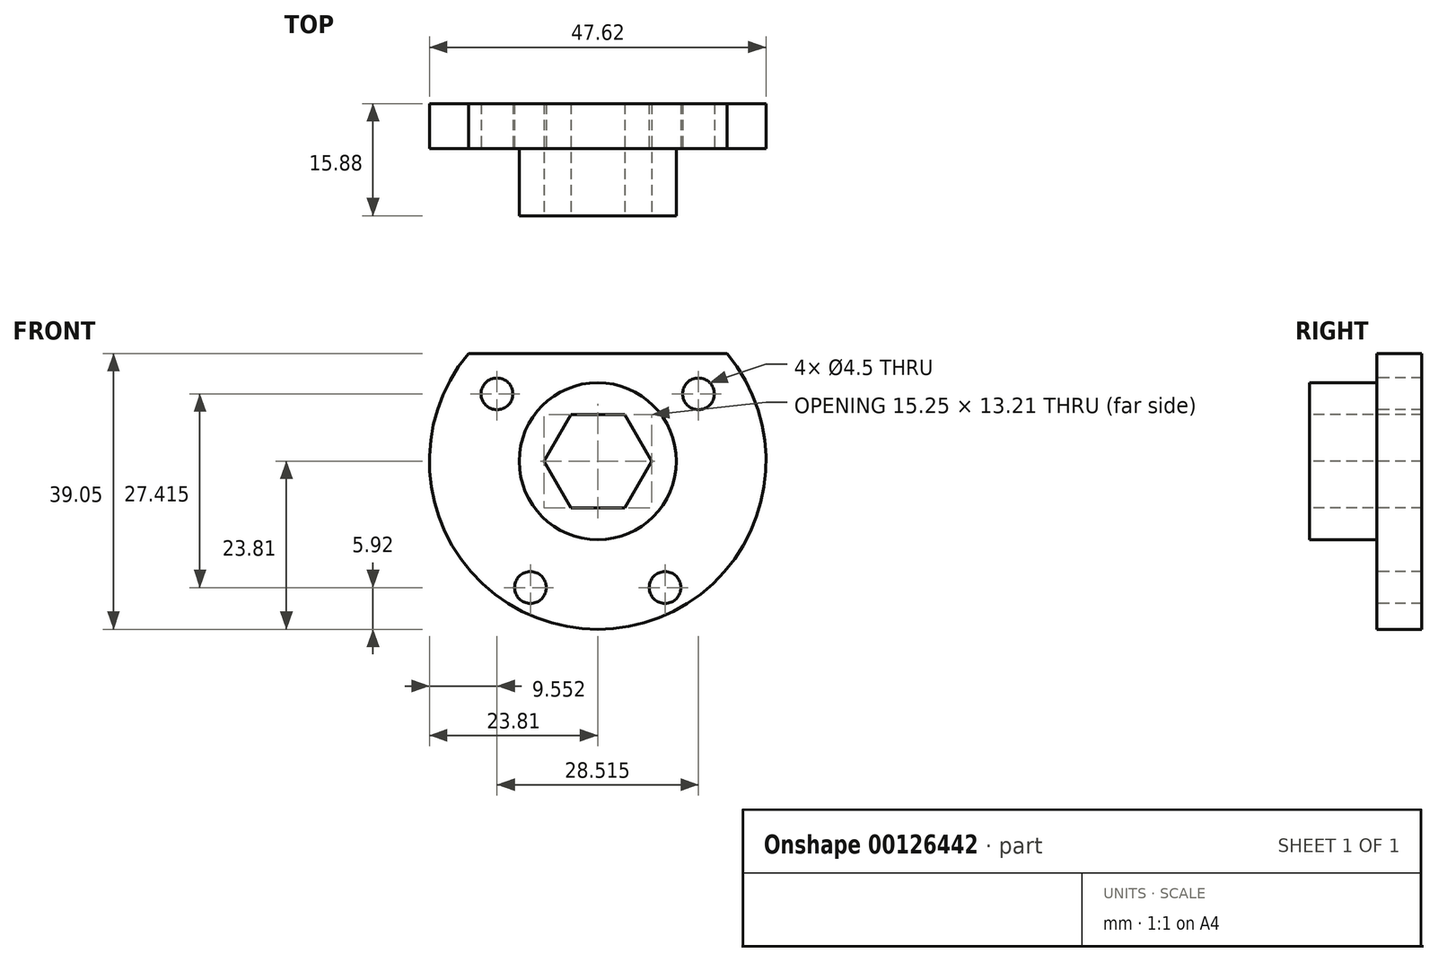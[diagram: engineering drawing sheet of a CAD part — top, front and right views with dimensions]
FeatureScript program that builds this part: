
annotation { "Feature Type Name" : "Feature", "Feature Type Description" : "" }
export const myFeature = defineFeature(function(context is Context, id is Id, definition is map)
    precondition{}
    {
        {
            var Q0;
            Q0=qCreatedBy(makeId("Front.planeOp"),FACE);
            var sketch = newSketch(context, id + "F0", { "sketchPlane" : qUnion([Q0])});
            skArc(sketch, "E0", {"start": v(-18.3, 15.24) * mm, "mid": v(0, -23.81) * mm, "end": v(18.3, 15.24) * mm});
            skLineSegment(sketch, "E1", {"start": v(-18.3, 15.24) * mm, "end": v(18.3, 15.24) * mm});
            skSolve(sketch);
        }
        {
            var Q0;
            Q0=makeQuery(id+"F0.imprint","IMPRINT",FACE,{"disambiguationData":[TD([[makeQuery(id+"F0.imprint","IMPRINT",EDGE,{"derivedFrom":sQuery(id+"F0.wireOp",EDGE,"E0")}),1.0]])]});
            extrude(context, id + "F1", {"entities" : qUnion([Q0]), "depth" : 6.35 * mm});
        }
        {
            var Q0;
            Q0=makeQuery(id+"F1.opExtrude","CAP_FACE",FACE,{"disambiguationData":[OSD([sQuery(id+"F0.wireOp",EDGE,"E0"),sQuery(id+"F0.wireOp",EDGE,"E1")])],"isStart":false});
            var sketch = newSketch(context, id + "F2", { "sketchPlane" : qUnion([Q0])});
            skCircle(sketch, "E2", {"center": v(0, -2.13) * mm, "radius": 18.41 * mm, "construction": true});
            skPoint(sketch, "E3", {"position": v(-14.26, 9.53) * mm});
            skPoint(sketch, "E4", {"position": v(-9.53, -17.9) * mm});
            skPoint(sketch, "E5", {"position": v(9.53, -17.9) * mm});
            skPoint(sketch, "E6", {"position": v(14.26, 9.53) * mm});
            skSolve(sketch);
        }
        {
            var Q0;
            Q0=sQuery(id+"F2.wireOp",VERTEX,"E3");
            var Q1;
            Q1=sQuery(id+"F2.wireOp",VERTEX,"E6");
            var Q2;
            Q2=sQuery(id+"F2.wireOp",VERTEX,"E5");
            var Q3;
            Q3=sQuery(id+"F2.wireOp",VERTEX,"E4");
            var Q4;
            Q4=makeQuery(id+"F1.opExtrude","SWEPT_BODY",BODY,{"disambiguationData":[OSD([sQuery(id+"F0.wireOp",EDGE,"E0"),sQuery(id+"F0.wireOp",EDGE,"E1")])]});
            hole(context, id + "F3", {"style" : HoleStyle.SIMPLE, "endStyle" : HoleEndStyle.THROUGH, "standardTappedOrClearance" : lookupTablePath({ "standard" : "ANSI", "fit" : "Normal (ASME)", "size" : "#8", "type" : "Clearance" }), "standardBlindInLast" : lookupTablePath({ "fit" : "Free", "standard" : "ANSI", "size" : "#8", "type" : "Clearance" }), "holeDiameter" : 4.5 * mm, "locations" : qUnion([Q0, Q1, Q2, Q3]), "scope" : qUnion([Q4]), "isTappedThrough" : true});
        }
        {
            var Q0;
            Q0=makeQuery(id+"F1.opExtrude","CAP_FACE",FACE,{"disambiguationData":[OSD([sQuery(id+"F0.wireOp",EDGE,"E0"),sQuery(id+"F0.wireOp",EDGE,"E1")])],"isStart":false});
            var sketch = newSketch(context, id + "F4", { "sketchPlane" : qUnion([Q0])});
            skCircle(sketch, "E7", {"center": v(0, 0) * mm, "radius": 11.11 * mm});
            skSolve(sketch);
        }
        {
            var Q0;
            Q0=makeQuery(id+"F4.imprint","IMPRINT",FACE,{"disambiguationData":[TD([[makeQuery(id+"F4.imprint","IMPRINT",EDGE,{"derivedFrom":sQuery(id+"F4.wireOp",EDGE,"E7")}),1.0]])]});
            extrude(context, id + "F5", {"entities" : qUnion([Q0]), "operationType" : NewBodyOperationType.ADD, "depth" : 9.52 * mm});
        }
        {
            var Q0;
            Q0=makeQuery(id+"F5.opExtrude","CAP_FACE",FACE,{"disambiguationData":[OSD([sQuery(id+"F4.wireOp",EDGE,"E7")])],"isStart":false});
            var sketch = newSketch(context, id + "F6", { "sketchPlane" : qUnion([Q0])});
            skCircle(sketch, "E8.cCircle", {"center": v(0, 0) * mm, "radius": 6.6 * mm, "construction": true});
            skLineSegment(sketch, "E8.0", {"start": v(7.63, 0) * mm, "end": v(3.81, -6.6) * mm});
            skLineSegment(sketch, "E8.1", {"start": v(3.81, -6.6) * mm, "end": v(-3.81, -6.6) * mm});
            skLineSegment(sketch, "E8.2", {"start": v(-3.81, -6.6) * mm, "end": v(-7.63, 0) * mm});
            skLineSegment(sketch, "E8.3", {"start": v(-7.63, 0) * mm, "end": v(-3.81, 6.6) * mm});
            skLineSegment(sketch, "E8.4", {"start": v(-3.81, 6.6) * mm, "end": v(3.81, 6.6) * mm});
            skLineSegment(sketch, "E8.5", {"start": v(3.81, 6.6) * mm, "end": v(7.63, 0) * mm});
            skSolve(sketch);
        }
        {
            var Q0;
            Q0 = qSketchRegion(id + "F6", true);
            extrude(context, id + "F7", {"entities" : qUnion([Q0]), "operationType" : NewBodyOperationType.REMOVE, "endBound" : BoundingType.THROUGH_ALL, "oppositeDirection" : true, "depth" : 25.4 * mm});
        }
    });
